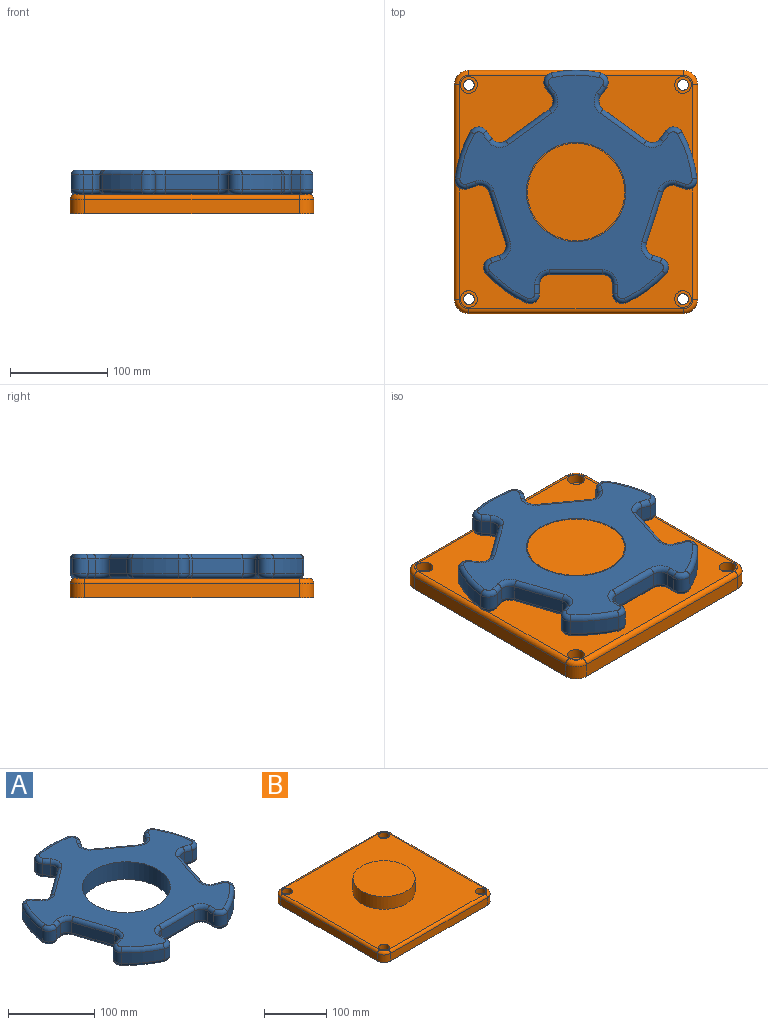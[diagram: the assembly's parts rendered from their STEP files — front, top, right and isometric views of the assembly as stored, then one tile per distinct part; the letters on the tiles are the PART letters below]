
ASSEMBLY  parts=2 mates=1
PART A: 123 faces, bbox 268.9x258.5x25 mm
  f0: plane 238.57x229.73mm, normal (0,0,1), area 21505.7mm2, adj f6,f43,f44,f45,f46,f47,f48,f49
  f1: plane 238.57x229.73mm, normal (0,0,-1), area 21505.7mm2, adj f6,f83,f84,f85,f86,f87,f88,f89
  f2: cylinder r=125mm len=40.68mm, axis (0,0,-1), area 759.5mm2, adj f13,f42,f51,f91
  f3: cylinder r=125mm len=47.82mm, axis (0,0,-1), area 759.5mm2, adj f35,f41,f67,f107
  f4: cylinder r=125mm len=50.29mm, axis (0,0,-1), area 759.5mm2, adj f28,f34,f82,f122
  f5: cylinder r=125mm len=47.82mm, axis (0,0,-1), area 759.5mm2, adj f21,f27,f66,f106
  f6: cylinder r=51mm len=102mm, axis (0,0,-1), area 8011.1mm2, adj f0,f1
  f7: cylinder r=125mm len=40.68mm, axis (0,0,-1), area 759.5mm2, adj f14,f20,f50,f90
  f8: plane 15x9.73mm, normal (-1,0,0), area 146mm2, adj f11,f14,f46,f86
  f9: plane 55x15mm, normal (0,-1,0), area 825mm2, adj f11,f12,f43,f83
  f10: plane 15x9.73mm, normal (1,0,0), area 146mm2, adj f12,f13,f47,f87
  f11: cylinder r=10mm len=15mm, axis (0,0,-1), area 235.6mm2, adj f8,f9,f44,f84
  f12: cylinder r=10mm len=15mm, axis (0,0,-1), area 235.6mm2, adj f9,f10,f45,f85
  f13: cylinder r=10mm len=15mm, axis (0,0,-1), area 299.5mm2, adj f2,f10,f49,f89
  f14: cylinder r=10mm len=15mm, axis (0,0,-1), area 299.5mm2, adj f7,f8,f48,f88
  f15: plane 15x9.26mm, normal (-0.31,-0.95,0), area 146mm2, adj f18,f21,f62,f102
  f16: plane 52.31x17mm, normal (0.95,-0.31,0), area 825mm2, adj f18,f19,f58,f98
  f17: plane 15x9.26mm, normal (0.31,0.95,0), area 146mm2, adj f19,f20,f54,f94
  f18: cylinder r=10mm len=15mm, axis (0,0,-1), area 235.6mm2, adj f15,f16,f60,f100
  f19: cylinder r=10mm len=15mm, axis (0,0,-1), area 235.6mm2, adj f16,f17,f56,f96
  f20: cylinder r=10mm len=16.25mm, axis (0,0,-1), area 299.5mm2, adj f7,f17,f52,f92
  f21: cylinder r=10mm len=15mm, axis (0,0,-1), area 299.5mm2, adj f5,f15,f64,f104
  f22: plane 15x7.87mm, normal (0.81,-0.59,0), area 146mm2, adj f25,f28,f78,f118
  f23: plane 44.5x32.33mm, normal (0.59,0.81,0), area 825mm2, adj f25,f26,f74,f114
  f24: plane 15x7.87mm, normal (-0.81,0.59,0), area 146mm2, adj f26,f27,f70,f110
  f25: cylinder r=10mm len=15mm, axis (0,0,-1), area 235.6mm2, adj f22,f23,f76,f116
  f26: cylinder r=10mm len=15mm, axis (0,0,-1), area 235.6mm2, adj f23,f24,f72,f112
  f27: cylinder r=10mm len=16.78mm, axis (0,0,-1), area 299.5mm2, adj f5,f24,f68,f108
  f28: cylinder r=10mm len=15.67mm, axis (0,0,-1), area 299.5mm2, adj f4,f22,f80,f120
  f29: plane 15x7.87mm, normal (0.81,0.59,0), area 146mm2, adj f32,f35,f71,f111
  f30: plane 44.5x32.33mm, normal (-0.59,0.81,0), area 825mm2, adj f32,f33,f75,f115
  f31: plane 15x7.87mm, normal (-0.81,-0.59,0), area 146mm2, adj f33,f34,f79,f119
  f32: cylinder r=10mm len=15mm, axis (0,0,-1), area 235.6mm2, adj f29,f30,f73,f113
  f33: cylinder r=10mm len=15mm, axis (0,0,-1), area 235.6mm2, adj f30,f31,f77,f117
  f34: cylinder r=10mm len=15.67mm, axis (0,0,-1), area 299.5mm2, adj f4,f31,f81,f121
  f35: cylinder r=10mm len=16.78mm, axis (0,0,-1), area 299.5mm2, adj f3,f29,f69,f109
  f36: plane 15x9.26mm, normal (-0.31,0.95,0), area 146mm2, adj f39,f42,f55,f95
  f37: plane 52.31x17mm, normal (-0.95,-0.31,0), area 825mm2, adj f39,f40,f59,f99
  f38: plane 15x9.26mm, normal (0.31,-0.95,0), area 146mm2, adj f40,f41,f63,f103
  f39: cylinder r=10mm len=15mm, axis (0,0,-1), area 235.6mm2, adj f36,f37,f57,f97
  f40: cylinder r=10mm len=15mm, axis (0,0,-1), area 235.6mm2, adj f37,f38,f61,f101
  f41: cylinder r=10mm len=15mm, axis (0,0,-1), area 299.5mm2, adj f3,f38,f65,f105
  f42: cylinder r=10mm len=16.25mm, axis (0,0,-1), area 299.5mm2, adj f2,f36,f53,f93
  f43: cylinder r=5mm len=55mm, axis (1,0,0), area 432mm2, adj f0,f9,f44,f45
  f44: torus R=15mm, axis (0,0,1), area 145.8mm2, adj f0,f11,f43,f46
  f45: torus R=15mm, axis (0,0,1), area 145.8mm2, adj f0,f12,f43,f47
  f46: cylinder r=5mm len=9.73mm, axis (0,-1,0), area 76.4mm2, adj f0,f8,f44,f48
  f47: cylinder r=5mm len=9.73mm, axis (0,1,0), area 76.4mm2, adj f0,f10,f45,f49
  f48: torus R=5mm, axis (0,0,1), area 128.3mm2, adj f0,f14,f46,f50
  f49: torus R=5mm, axis (0,0,1), area 128.3mm2, adj f0,f13,f47,f51
  f50: torus R=120mm, axis (0,0,1), area 391.9mm2, adj f0,f7,f48,f52
  f51: torus R=120mm, axis (0,0,1), area 391.9mm2, adj f0,f2,f49,f53
  f52: torus R=5mm, axis (0,0,1), area 128.3mm2, adj f0,f20,f50,f54
  f53: torus R=5mm, axis (0,0,1), area 128.3mm2, adj f0,f42,f51,f55
  f54: cylinder r=5mm len=10.8mm, axis (-0.95,0.31,0), area 76.4mm2, adj f0,f17,f52,f56
  f55: cylinder r=5mm len=10.8mm, axis (-0.95,-0.31,0), area 76.4mm2, adj f0,f36,f53,f57
  f56: torus R=15mm, axis (0,0,1), area 145.8mm2, adj f0,f19,f54,f58
  f57: torus R=15mm, axis (0,0,1), area 145.8mm2, adj f0,f39,f55,f59
  f58: cylinder r=5mm len=53.85mm, axis (0.31,0.95,0), area 432mm2, adj f0,f16,f56,f60
  f59: cylinder r=5mm len=53.85mm, axis (0.31,-0.95,0), area 432mm2, adj f0,f37,f57,f61
  f60: torus R=15mm, axis (0,0,1), area 145.8mm2, adj f0,f18,f58,f62
  f61: torus R=15mm, axis (0,0,1), area 145.8mm2, adj f0,f40,f59,f63
  f62: cylinder r=5mm len=10.8mm, axis (0.95,-0.31,0), area 76.4mm2, adj f0,f15,f60,f64
  f63: cylinder r=5mm len=10.8mm, axis (0.95,0.31,0), area 76.4mm2, adj f0,f38,f61,f65
  f64: torus R=5mm, axis (0,0,1), area 128.3mm2, adj f0,f21,f62,f66
  f65: torus R=5mm, axis (0,0,1), area 128.3mm2, adj f0,f41,f63,f67
  f66: torus R=120mm, axis (0,0,1), area 391.9mm2, adj f0,f5,f64,f68
  f67: torus R=120mm, axis (0,0,1), area 391.9mm2, adj f0,f3,f65,f69
  f68: torus R=5mm, axis (0,0,1), area 128.3mm2, adj f0,f27,f66,f70
  f69: torus R=5mm, axis (0,0,1), area 128.3mm2, adj f0,f35,f67,f71
  f70: cylinder r=5mm len=10.81mm, axis (-0.59,-0.81,0), area 76.4mm2, adj f0,f24,f68,f72
  f71: cylinder r=5mm len=10.81mm, axis (-0.59,0.81,0), area 76.4mm2, adj f0,f29,f69,f73
  f72: torus R=15mm, axis (0,0,1), area 145.8mm2, adj f0,f26,f70,f74
  f73: torus R=15mm, axis (0,0,1), area 145.8mm2, adj f0,f32,f71,f75
  f74: cylinder r=5mm len=47.44mm, axis (-0.81,0.59,0), area 432mm2, adj f0,f23,f72,f76
  f75: cylinder r=5mm len=47.44mm, axis (-0.81,-0.59,0), area 432mm2, adj f0,f30,f73,f77
  f76: torus R=15mm, axis (0,0,1), area 145.8mm2, adj f0,f25,f74,f78
  f77: torus R=15mm, axis (0,0,1), area 145.8mm2, adj f0,f33,f75,f79
  f78: cylinder r=5mm len=10.81mm, axis (0.59,0.81,0), area 76.4mm2, adj f0,f22,f76,f80
  f79: cylinder r=5mm len=10.81mm, axis (0.59,-0.81,0), area 76.4mm2, adj f0,f31,f77,f81
  f80: torus R=5mm, axis (0,0,1), area 128.3mm2, adj f0,f28,f78,f82
  f81: torus R=5mm, axis (0,0,1), area 128.3mm2, adj f0,f34,f79,f82
  f82: torus R=120mm, axis (0,0,1), area 391.9mm2, adj f0,f4,f80,f81
  f83: cylinder r=5mm len=55mm, axis (-1,0,0), area 432mm2, adj f1,f9,f84,f85
  f84: torus R=15mm, axis (0,0,1), area 145.8mm2, adj f1,f11,f83,f86
  f85: torus R=15mm, axis (0,0,1), area 145.8mm2, adj f1,f12,f83,f87
  f86: cylinder r=5mm len=9.73mm, axis (0,1,0), area 76.4mm2, adj f1,f8,f84,f88
  f87: cylinder r=5mm len=9.73mm, axis (0,-1,0), area 76.4mm2, adj f1,f10,f85,f89
  f88: torus R=5mm, axis (0,0,1), area 128.3mm2, adj f1,f14,f86,f90
  f89: torus R=5mm, axis (0,0,1), area 128.3mm2, adj f1,f13,f87,f91
  f90: torus R=120mm, axis (0,0,1), area 391.9mm2, adj f1,f7,f88,f92
  f91: torus R=120mm, axis (0,0,1), area 391.9mm2, adj f1,f2,f89,f93
  f92: torus R=5mm, axis (0,0,1), area 128.3mm2, adj f1,f20,f90,f94
  f93: torus R=5mm, axis (0,0,1), area 128.3mm2, adj f1,f42,f91,f95
  f94: cylinder r=5mm len=10.8mm, axis (0.95,-0.31,0), area 76.4mm2, adj f1,f17,f92,f96
  f95: cylinder r=5mm len=10.8mm, axis (0.95,0.31,0), area 76.4mm2, adj f1,f36,f93,f97
  f96: torus R=15mm, axis (0,0,1), area 145.8mm2, adj f1,f19,f94,f98
  f97: torus R=15mm, axis (0,0,1), area 145.8mm2, adj f1,f39,f95,f99
  f98: cylinder r=5mm len=53.85mm, axis (-0.31,-0.95,0), area 432mm2, adj f1,f16,f96,f100
  f99: cylinder r=5mm len=53.85mm, axis (-0.31,0.95,0), area 432mm2, adj f1,f37,f97,f101
  f100: torus R=15mm, axis (0,0,1), area 145.8mm2, adj f1,f18,f98,f102
  f101: torus R=15mm, axis (0,0,1), area 145.8mm2, adj f1,f40,f99,f103
  f102: cylinder r=5mm len=10.8mm, axis (-0.95,0.31,0), area 76.4mm2, adj f1,f15,f100,f104
  f103: cylinder r=5mm len=10.8mm, axis (-0.95,-0.31,0), area 76.4mm2, adj f1,f38,f101,f105
  f104: torus R=5mm, axis (0,0,1), area 128.3mm2, adj f1,f21,f102,f106
  f105: torus R=5mm, axis (0,0,1), area 128.3mm2, adj f1,f41,f103,f107
  f106: torus R=120mm, axis (0,0,1), area 391.9mm2, adj f1,f5,f104,f108
  f107: torus R=120mm, axis (0,0,1), area 391.9mm2, adj f1,f3,f105,f109
  f108: torus R=5mm, axis (0,0,1), area 128.3mm2, adj f1,f27,f106,f110
  f109: torus R=5mm, axis (0,0,1), area 128.3mm2, adj f1,f35,f107,f111
  f110: cylinder r=5mm len=10.81mm, axis (0.59,0.81,0), area 76.4mm2, adj f1,f24,f108,f112
  f111: cylinder r=5mm len=10.81mm, axis (0.59,-0.81,0), area 76.4mm2, adj f1,f29,f109,f113
  f112: torus R=15mm, axis (0,0,1), area 145.8mm2, adj f1,f26,f110,f114
  f113: torus R=15mm, axis (0,0,1), area 145.8mm2, adj f1,f32,f111,f115
  f114: cylinder r=5mm len=47.44mm, axis (0.81,-0.59,0), area 432mm2, adj f1,f23,f112,f116
  f115: cylinder r=5mm len=47.44mm, axis (0.81,0.59,0), area 432mm2, adj f1,f30,f113,f117
  f116: torus R=15mm, axis (0,0,1), area 145.8mm2, adj f1,f25,f114,f118
  f117: torus R=15mm, axis (0,0,1), area 145.8mm2, adj f1,f33,f115,f119
  f118: cylinder r=5mm len=10.81mm, axis (-0.59,-0.81,0), area 76.4mm2, adj f1,f22,f116,f120
  f119: cylinder r=5mm len=10.81mm, axis (-0.59,0.81,0), area 76.4mm2, adj f1,f31,f117,f121
  f120: torus R=5mm, axis (0,0,1), area 128.3mm2, adj f1,f28,f118,f122
  f121: torus R=5mm, axis (0,0,1), area 128.3mm2, adj f1,f34,f119,f122
  f122: torus R=120mm, axis (0,0,1), area 391.9mm2, adj f1,f4,f120,f121
PART B: 32 faces, bbox 252.5x252.5x45 mm
  f0: plane 220x15mm, normal (1,0,0), area 3300mm2, adj f5,f8,f11,f27
  f1: plane 220x15mm, normal (0,1,0), area 3300mm2, adj f5,f8,f9,f31
  f2: plane 220x15mm, normal (-1,0,0), area 3300mm2, adj f5,f9,f10,f28
  f3: plane 220x15mm, normal (0,-1,0), area 3300mm2, adj f5,f10,f11,f24
  f4: plane 240x240mm, normal (0,0,1), area 48725.4mm2, adj f6,f14,f17,f20,f23,f24,f25,f26
  f5: plane 250x250mm, normal (0,0,-1), area 61926.7mm2, adj f0,f1,f2,f3,f8,f9,f10,f11
  f6: cylinder r=50mm len=100mm, axis (0,0,-1), area 7854mm2, adj f4,f7
  f7: plane 100x100mm, normal (0,0,1), area 7854mm2, adj f6
  f8: cylinder r=15mm len=15mm, axis (0,0,-1), area 353.4mm2, adj f0,f1,f5,f29
  f9: cylinder r=15mm len=15mm, axis (0,0,1), area 353.4mm2, adj f1,f2,f5,f30
  f10: cylinder r=15mm len=15mm, axis (0,0,-1), area 353.4mm2, adj f2,f3,f5,f26
  f11: cylinder r=15mm len=15mm, axis (0,0,1), area 353.4mm2, adj f0,f3,f5,f25
  f12: cylinder r=5.5mm len=11mm, axis (0,0,1), area 345.6mm2, adj f5,f13
  f13: plane 17.25x17.25mm, normal (0,0,1), area 138.7mm2, adj f12,f14
  f14: cylinder r=8.62mm len=17.25mm, axis (0,0,1), area 541.9mm2, adj f4,f13
  f15: cylinder r=5.5mm len=11mm, axis (0,0,1), area 345.6mm2, adj f5,f16
  f16: plane 17.25x17.25mm, normal (0,0,1), area 138.7mm2, adj f15,f17
  f17: cylinder r=8.62mm len=17.25mm, axis (0,0,1), area 541.9mm2, adj f4,f16
  f18: cylinder r=5.5mm len=11mm, axis (0,0,1), area 345.6mm2, adj f5,f19
  f19: plane 17.25x17.25mm, normal (0,0,1), area 138.7mm2, adj f18,f20
  f20: cylinder r=8.62mm len=17.25mm, axis (0,0,1), area 541.9mm2, adj f4,f19
  f21: cylinder r=5.5mm len=11mm, axis (0,0,1), area 345.6mm2, adj f5,f22
  f22: plane 17.25x17.25mm, normal (0,0,1), area 138.7mm2, adj f21,f23
  f23: cylinder r=8.62mm len=17.25mm, axis (0,0,1), area 541.9mm2, adj f4,f22
  f24: cylinder r=5mm len=220mm, axis (-1,0,0), area 1727.9mm2, adj f3,f4,f25,f26
  f25: torus R=10mm, axis (0,0,1), area 162.6mm2, adj f4,f11,f24,f27
  f26: torus R=10mm, axis (0,0,1), area 162.6mm2, adj f4,f10,f24,f28
  f27: cylinder r=5mm len=220mm, axis (0,-1,0), area 1727.9mm2, adj f0,f4,f25,f29
  f28: cylinder r=5mm len=220mm, axis (0,1,0), area 1727.9mm2, adj f2,f4,f26,f30
  f29: torus R=10mm, axis (0,0,1), area 162.6mm2, adj f4,f8,f27,f31
  f30: torus R=10mm, axis (0,0,1), area 162.6mm2, adj f4,f9,f28,f31
  f31: cylinder r=5mm len=220mm, axis (1,0,0), area 1727.9mm2, adj f1,f4,f29,f30
PLACE A at identity
PLACE B at identity fixed
MATE revolute B.f6 <-> A.f2  axis (0,0,1) through (0,0,45)mm
